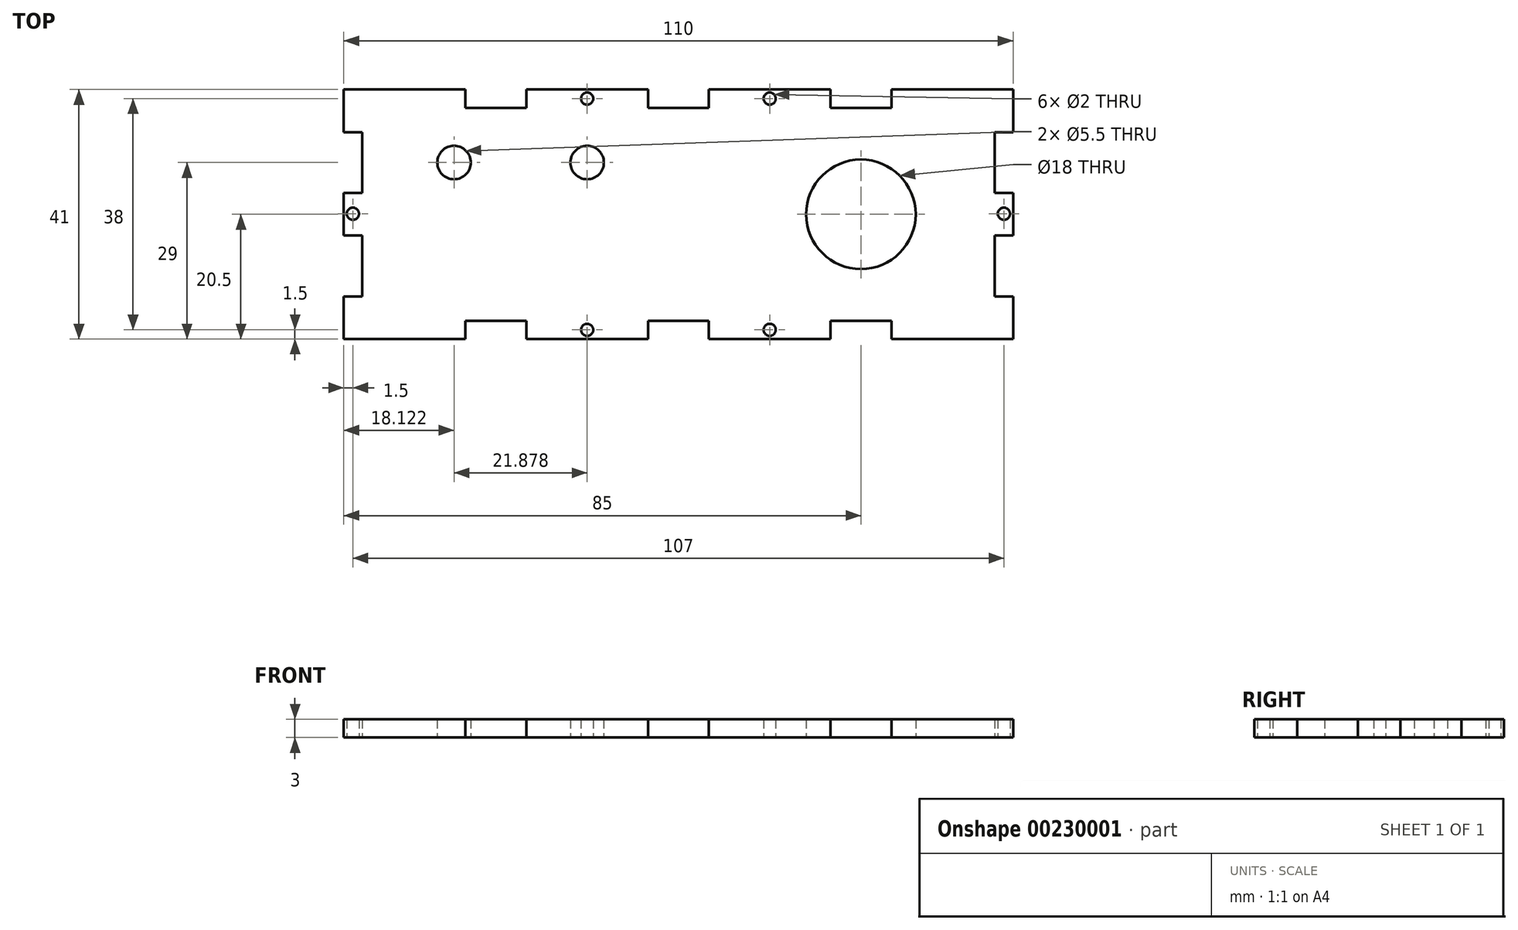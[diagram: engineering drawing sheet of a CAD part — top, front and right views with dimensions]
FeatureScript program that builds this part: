
annotation { "Feature Type Name" : "Feature", "Feature Type Description" : "" }
export const myFeature = defineFeature(function(context is Context, id is Id, definition is map)
    precondition{}
    {
        {
            var Q0;
            Q0=qCreatedBy(makeId("Top.planeOp"),FACE);
            var sketch = newSketch(context, id + "F0", { "sketchPlane" : qUnion([Q0])});
            skLineSegment(sketch, "E0", {"start": v(0, 0) * mm, "end": v(0, 7) * mm});
            skLineSegment(sketch, "E1", {"start": v(0, 7) * mm, "end": v(3, 7) * mm});
            skLineSegment(sketch, "E2", {"start": v(3, 7) * mm, "end": v(3, 17) * mm});
            skLineSegment(sketch, "E3", {"start": v(3, 17) * mm, "end": v(0, 17) * mm});
            skLineSegment(sketch, "E4", {"start": v(0, 17) * mm, "end": v(0, 24) * mm});
            skLineSegment(sketch, "E5", {"start": v(0, 24) * mm, "end": v(3, 24) * mm});
            skLineSegment(sketch, "E6", {"start": v(3, 24) * mm, "end": v(3, 34) * mm});
            skLineSegment(sketch, "E7", {"start": v(3, 34) * mm, "end": v(0, 34) * mm});
            skLineSegment(sketch, "E8", {"start": v(0, 34) * mm, "end": v(0, 41) * mm});
            skLineSegment(sketch, "E9", {"start": v(0, 41) * mm, "end": v(20, 41) * mm});
            skLineSegment(sketch, "E10", {"start": v(20, 41) * mm, "end": v(20, 38) * mm});
            skLineSegment(sketch, "E11", {"start": v(20, 38) * mm, "end": v(30, 38) * mm});
            skLineSegment(sketch, "E12", {"start": v(30, 38) * mm, "end": v(30, 41) * mm});
            skLineSegment(sketch, "E13", {"start": v(30, 41) * mm, "end": v(50, 41) * mm});
            skLineSegment(sketch, "E14", {"start": v(50, 41) * mm, "end": v(50, 38) * mm});
            skLineSegment(sketch, "E15", {"start": v(50, 38) * mm, "end": v(55, 38) * mm});
            skLineSegment(sketch, "E16", {"start": v(0, 0) * mm, "end": v(20, 0) * mm});
            skLineSegment(sketch, "E17", {"start": v(20, 0) * mm, "end": v(20, 3) * mm});
            skLineSegment(sketch, "E18", {"start": v(20, 3) * mm, "end": v(30, 3) * mm});
            skLineSegment(sketch, "E19", {"start": v(30, 3) * mm, "end": v(30, 0) * mm});
            skLineSegment(sketch, "E20", {"start": v(30, 0) * mm, "end": v(50, 0) * mm});
            skLineSegment(sketch, "E21", {"start": v(50, 0) * mm, "end": v(50, 3) * mm});
            skLineSegment(sketch, "E22", {"start": v(50, 3) * mm, "end": v(55, 3) * mm});
            skLineSegment(sketch, "E23", {"start": v(55, 38) * mm, "end": v(55, 3) * mm, "construction": true});
            skLineSegment(sketch, "E24.MirrorCS", {"start": v(110, 7) * mm, "end": v(107, 7) * mm});
            skLineSegment(sketch, "E25.MirrorCS", {"start": v(107, 17) * mm, "end": v(110, 17) * mm});
            skLineSegment(sketch, "E26.MirrorCS", {"start": v(107, 34) * mm, "end": v(110, 34) * mm});
            skLineSegment(sketch, "E27.MirrorCS", {"start": v(110, 24) * mm, "end": v(107, 24) * mm});
            skLineSegment(sketch, "E28.MirrorCS", {"start": v(80, 3) * mm, "end": v(80, 0) * mm});
            skLineSegment(sketch, "E29.MirrorCS", {"start": v(60, 0) * mm, "end": v(60, 3) * mm});
            skLineSegment(sketch, "E30.MirrorCS", {"start": v(90, 41) * mm, "end": v(90, 38) * mm});
            skLineSegment(sketch, "E31.MirrorCS", {"start": v(60, 41) * mm, "end": v(60, 38) * mm});
            skLineSegment(sketch, "E32.MirrorCS", {"start": v(90, 0) * mm, "end": v(90, 3) * mm});
            skLineSegment(sketch, "E33.MirrorCS", {"start": v(80, 38) * mm, "end": v(80, 41) * mm});
            skLineSegment(sketch, "E34.MirrorCS", {"start": v(110, 0) * mm, "end": v(110, 7) * mm});
            skLineSegment(sketch, "E35.MirrorCS", {"start": v(107, 7) * mm, "end": v(107, 17) * mm});
            skLineSegment(sketch, "E36.MirrorCS", {"start": v(110, 34) * mm, "end": v(110, 41) * mm});
            skLineSegment(sketch, "E37.MirrorCS", {"start": v(110, 0) * mm, "end": v(90, 0) * mm});
            skLineSegment(sketch, "E38.MirrorCS", {"start": v(90, 3) * mm, "end": v(80, 3) * mm});
            skLineSegment(sketch, "E39.MirrorCS", {"start": v(60, 3) * mm, "end": v(55, 3) * mm});
            skLineSegment(sketch, "E40.MirrorCS", {"start": v(80, 0) * mm, "end": v(60, 0) * mm});
            skLineSegment(sketch, "E41.MirrorCS", {"start": v(107, 24) * mm, "end": v(107, 34) * mm});
            skLineSegment(sketch, "E42.MirrorCS", {"start": v(110, 17) * mm, "end": v(110, 24) * mm});
            skLineSegment(sketch, "E43.MirrorCS", {"start": v(110, 41) * mm, "end": v(90, 41) * mm});
            skLineSegment(sketch, "E44.MirrorCS", {"start": v(80, 41) * mm, "end": v(60, 41) * mm});
            skLineSegment(sketch, "E45.MirrorCS", {"start": v(60, 38) * mm, "end": v(55, 38) * mm});
            skLineSegment(sketch, "E46.MirrorCS", {"start": v(90, 38) * mm, "end": v(80, 38) * mm});
            skCircle(sketch, "E47", {"center": v(40, 39.5) * mm, "radius": 1 * mm});
            skPoint(sketch, "E47.centerSnap0", {"position": v(40, 41) * mm});
            skCircle(sketch, "E48.MirrorC", {"center": v(70, 39.5) * mm, "radius": 1 * mm});
            skLineSegment(sketch, "E49", {"start": v(0, 20.5) * mm, "end": v(55, 20.5) * mm, "construction": true});
            skCircle(sketch, "E50.MirrorC", {"center": v(40, 1.5) * mm, "radius": 1 * mm});
            skCircle(sketch, "E51.MirrorC", {"center": v(70, 1.5) * mm, "radius": 1 * mm});
            skCircle(sketch, "E52.MirrorC", {"center": v(1.5, 20.58) * mm, "radius": 1 * mm});
            skCircle(sketch, "E53.MirrorC", {"center": v(108.5, 20.58) * mm, "radius": 1 * mm});
            skPoint(sketch, "E54", {"position": v(3, 29) * mm});
            skCircle(sketch, "E55", {"center": v(40, 29) * mm, "radius": 2.75 * mm});
            skCircle(sketch, "E56", {"center": v(18.12, 29) * mm, "radius": 2.75 * mm});
            skLineSegment(sketch, "E57", {"start": v(110, 41) * mm, "end": v(60, 0) * mm, "construction": true});
            skLineSegment(sketch, "E58", {"start": v(60, 41) * mm, "end": v(110, 0) * mm, "construction": true});
            skCircle(sketch, "E59", {"center": v(85, 20.5) * mm, "radius": 9 * mm});
            skSolve(sketch);
        }
        {
            var Q0;
            Q0 = qSketchRegion(id + "F0", true);
            extrude(context, id + "F1", {"entities" : qUnion([Q0]), "depth" : 3 * mm});
        }
    });
